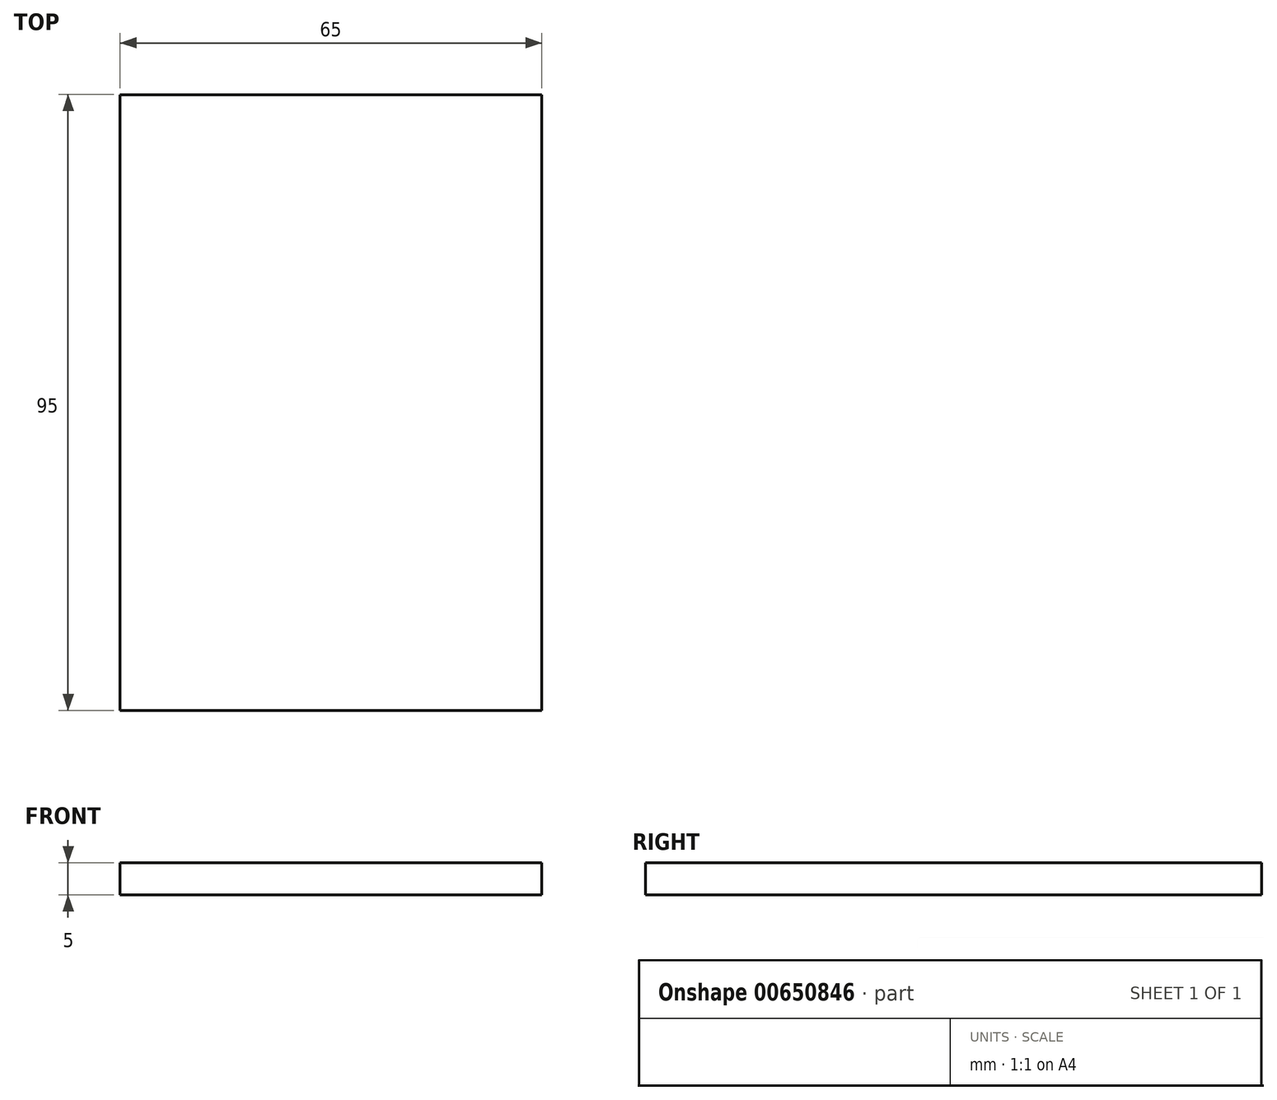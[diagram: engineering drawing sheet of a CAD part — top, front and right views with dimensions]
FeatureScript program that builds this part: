
annotation { "Feature Type Name" : "Feature", "Feature Type Description" : "" }
export const myFeature = defineFeature(function(context is Context, id is Id, definition is map)
    precondition{}
    {
        {
            var Q0;
            Q0=qCreatedBy(makeId("Top.planeOp"),FACE);
            var sketch = newSketch(context, id + "F0", { "sketchPlane" : qUnion([Q0])});
            skLineSegment(sketch, "E0.bottom", {"start": v(-32.63, 48.82) * mm, "end": v(32.37, 48.82) * mm});
            skLineSegment(sketch, "E0.top", {"start": v(-32.63, -46.18) * mm, "end": v(32.37, -46.18) * mm});
            skLineSegment(sketch, "E0.left", {"start": v(-32.63, 48.82) * mm, "end": v(-32.63, -46.18) * mm});
            skLineSegment(sketch, "E0.right", {"start": v(32.37, 48.82) * mm, "end": v(32.37, -46.18) * mm});
            skSolve(sketch);
        }
        {
            var Q0;
            Q0=makeQuery(id+"F0.imprint","IMPRINT",FACE,{"disambiguationData":[TD([[makeQuery(id+"F0.imprint","IMPRINT",EDGE,{"derivedFrom":sQuery(id+"F0.wireOp",EDGE,"E0.bottom")}),-1.0]])]});
            extrude(context, id + "F1", {"entities" : qUnion([Q0]), "depth" : 5 * mm, "offsetDistance" : 25.4 * mm});
        }
    });
